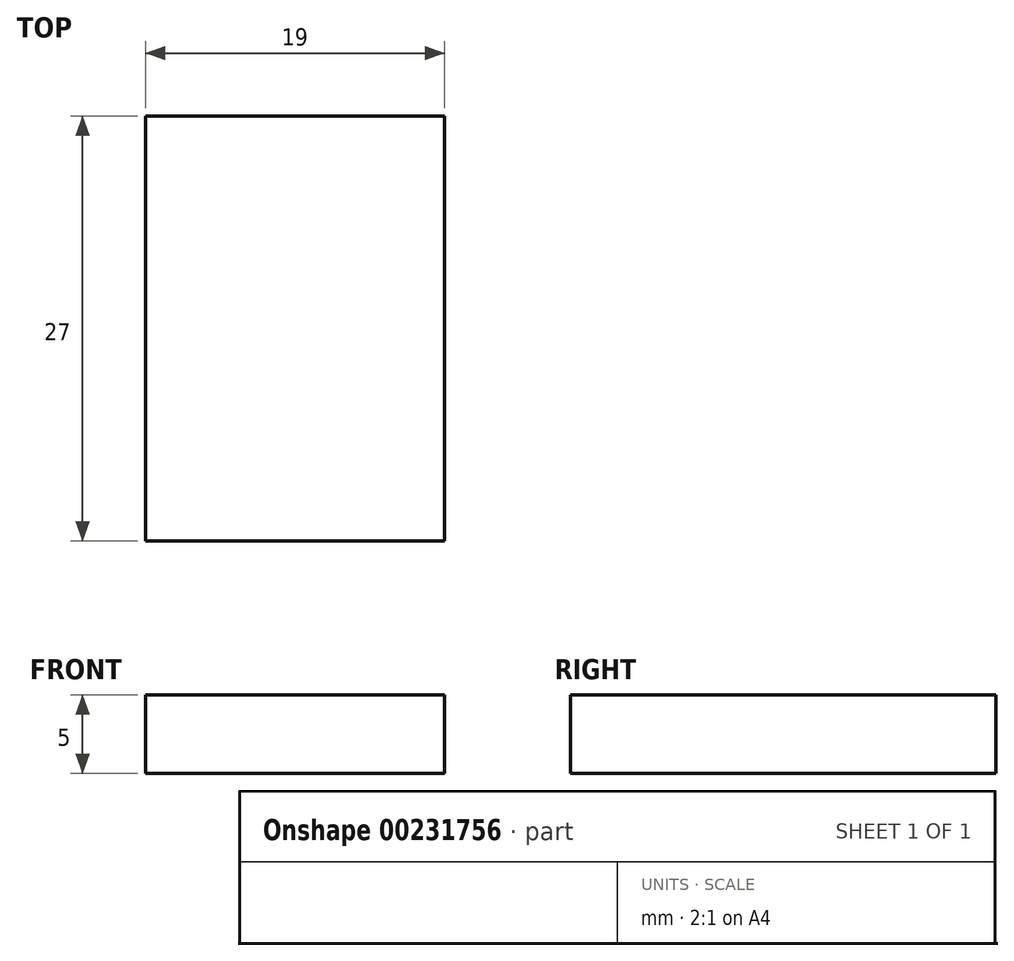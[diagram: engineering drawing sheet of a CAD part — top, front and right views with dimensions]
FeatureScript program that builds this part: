
annotation { "Feature Type Name" : "Feature", "Feature Type Description" : "" }
export const myFeature = defineFeature(function(context is Context, id is Id, definition is map)
    precondition{}
    {
        {
            var Q0;
            Q0=qCreatedBy(makeId("Top.planeOp"),FACE);
            var sketch = newSketch(context, id + "F0", { "sketchPlane" : qUnion([Q0])});
            skLineSegment(sketch, "E0.bottom", {"start": v(9.5, 13.5) * mm, "end": v(-9.5, 13.5) * mm});
            skLineSegment(sketch, "E0.top", {"start": v(9.5, -13.5) * mm, "end": v(-9.5, -13.5) * mm});
            skLineSegment(sketch, "E0.left", {"start": v(9.5, 13.5) * mm, "end": v(9.5, -13.5) * mm});
            skLineSegment(sketch, "E0.right", {"start": v(-9.5, 13.5) * mm, "end": v(-9.5, -13.5) * mm});
            skPoint(sketch, "E0.middle", {"position": v(0, 0) * mm});
            skSolve(sketch);
        }
        {
            var Q0;
            Q0=makeQuery(id+"F0.imprint","IMPRINT",FACE,{"disambiguationData":[TD([[makeQuery(id+"F0.imprint","IMPRINT",EDGE,{"derivedFrom":sQuery(id+"F0.wireOp",EDGE,"E0.bottom")}),1.0]])]});
            extrude(context, id + "F1", {"entities" : qUnion([Q0]), "depth" : 5 * mm});
        }
    });
